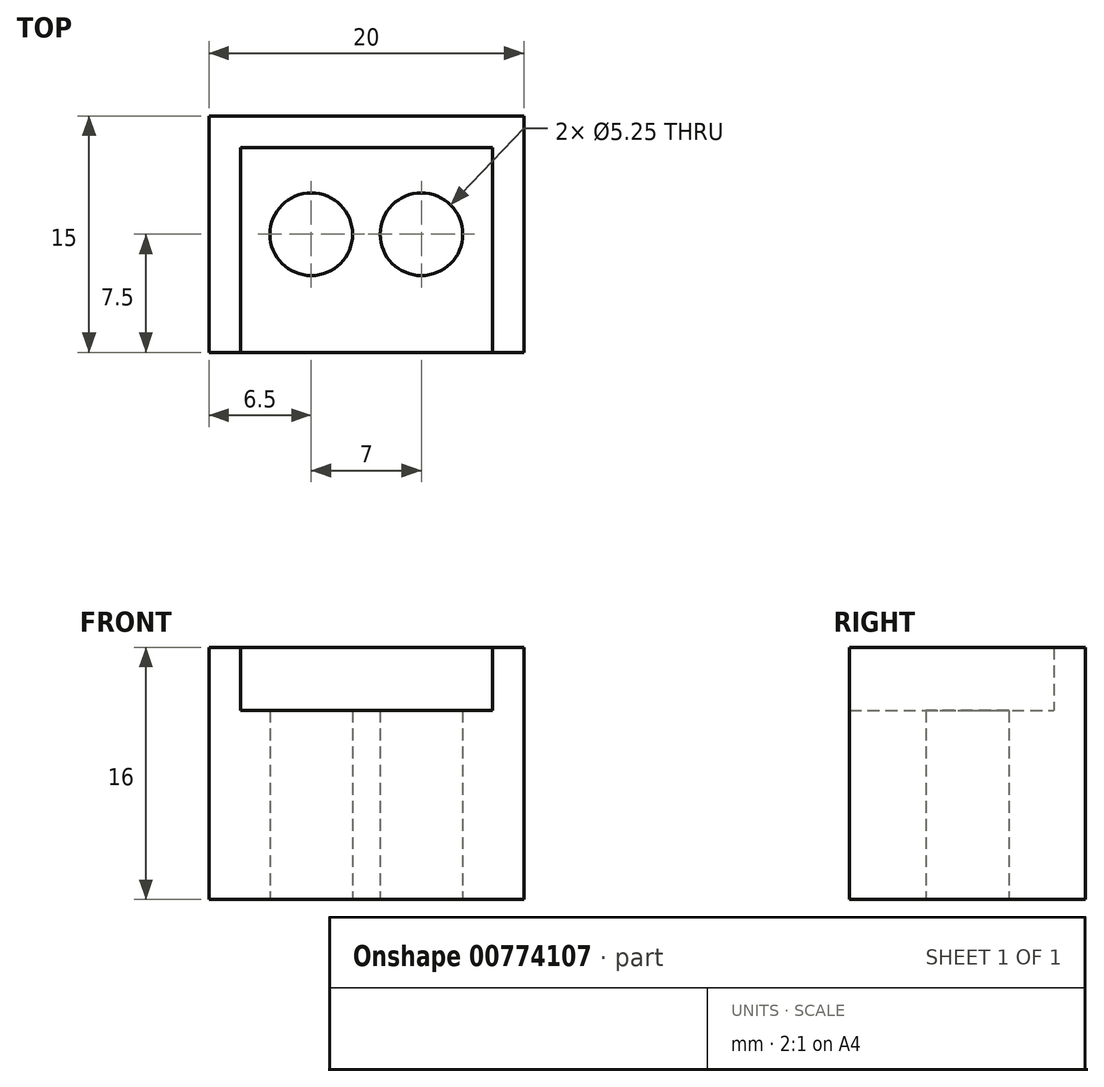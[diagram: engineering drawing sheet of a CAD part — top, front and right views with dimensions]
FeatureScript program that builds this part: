
annotation { "Feature Type Name" : "Feature", "Feature Type Description" : "" }
export const myFeature = defineFeature(function(context is Context, id is Id, definition is map)
    precondition{}
    {
        {
            var Q0;
            Q0=qCreatedBy(makeId("Top.planeOp"),FACE);
            var sketch = newSketch(context, id + "F0", { "sketchPlane" : qUnion([Q0])});
            skLineSegment(sketch, "E0.bottom", {"start": v(10, -7.5) * mm, "end": v(-10, -7.5) * mm});
            skLineSegment(sketch, "E0.top", {"start": v(10, 7.5) * mm, "end": v(-10, 7.5) * mm});
            skLineSegment(sketch, "E0.left", {"start": v(10, -7.5) * mm, "end": v(10, 7.5) * mm});
            skLineSegment(sketch, "E0.right", {"start": v(-10, -7.5) * mm, "end": v(-10, 7.5) * mm});
            skPoint(sketch, "E0.middle", {"position": v(0, 0) * mm});
            skCircle(sketch, "E1", {"center": v(-3.5, 0) * mm, "radius": 2.62 * mm});
            skPoint(sketch, "E1.centerSnap0", {"position": v(-10, 0) * mm});
            skCircle(sketch, "E2.MirrorC", {"center": v(3.5, 0) * mm, "radius": 2.62 * mm});
            skLineSegment(sketch, "E3.bottom", {"start": v(-8, -7.5) * mm, "end": v(8, -7.5) * mm});
            skLineSegment(sketch, "E3.top", {"start": v(-8, 5.5) * mm, "end": v(8, 5.5) * mm});
            skLineSegment(sketch, "E3.left", {"start": v(-8, -7.5) * mm, "end": v(-8, 5.5) * mm});
            skLineSegment(sketch, "E3.right", {"start": v(8, -7.5) * mm, "end": v(8, 5.5) * mm});
            skSolve(sketch);
        }
        {
            var Q0;
            Q0=makeQuery(id+"F0.imprint","IMPRINT",FACE,{"disambiguationData":[TD([[makeQuery(id+"F0.imprint","IMPRINT",EDGE,{"derivedFrom":sQuery(id+"F0.wireOp",EDGE,"E1")}),-1.0]])]});
            extrude(context, id + "F1", {"entities" : qUnion([Q0]), "depth" : 12 * mm, "offsetDistance" : 25 * mm});
        }
        {
            var Q0;
            Q0=makeQuery(id+"F0.imprint","IMPRINT",FACE,{"disambiguationData":[TD([[makeQuery(id+"F0.imprint","IMPRINT",EDGE,{"derivedFrom":sQuery(id+"F0.wireOp",EDGE,"E0.top")}),1.0]])]});
            extrude(context, id + "F2", {"entities" : qUnion([Q0]), "operationType" : NewBodyOperationType.ADD, "depth" : 16 * mm, "offsetDistance" : 25 * mm});
        }
    });
